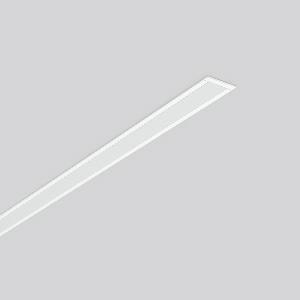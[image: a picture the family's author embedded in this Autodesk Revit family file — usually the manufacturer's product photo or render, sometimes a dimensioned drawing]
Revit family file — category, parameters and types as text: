
# Revit family: less_is_more_27_312176_002_1_76_0c9e
name_source: partatom
category: Lighting Fixtures
units: mm (PartAtom-declared; Revit-internal decimal feet)

## family parameters
Cut with Voids When Loaded = No
Host = Face
Light Source = No
Part Type = Normal
Room Calculation Point = No
Round Connector Dimension = Use Diameter
Shared = No

## types (1)
- LESS IS MORE 27 (1 x LED Modul 840, 1950 lm, 4000)
    Apparent Load = 25 VA
    CIE Flux Codes = 48 79 96 100 100
    Color Rendering = 80
    Color Temperature = 4000
    Default Elevation = 1800 mm
    Description = Series: LESS IS MORE 27
Recessed ceiling and wall luminaire with slim design. Housing: extruded aluminium profile, powder-coated. End cap aluminium powder-coated. Diffuser made of non-yellowing plastic (PMMA), opal. Suitable for Recessed ceiling mounting, wall (recessed). External driver with connecting cable. 
Colour: traffic white, matt (RAL 9016)
Length: 1014 mm
Width: 38 mm
Height: 2 mm
Cut-out length: 1006 mm
Cut-out width: 30 mm
Recess height: 45-60 mm
Luminaire: recess height: 37 mm
Lamp: LED
Socket: without socket
Colour temperature: 4000K
Colour rendering index (CRI): 82
System power: 25 W
Rated luminous flux: 1950 lm
Luminous efficiency: 78 lm/W
Control gear: Voltage converter, DALI dim.
Protection class: II
Type of protection: IP 20
    Height = 0 mm  [stored 0 ft]
    Lamp = 1 x LED Modul 840
    Lamp Light Flux = 1950 lm
    Lamp count = 1
    Length = 1014 mm
    Lifetime = 50000 h
    Luminous efficacy = 78 lm/W
    Manufacturer = RZB
    ModVariant = No
    Model = 312176.002.1.76
    Mounting Place = Ceiling, Wall
    Mounting Type = Recessed
    Number of Poles = 1
    OnlyDefault = Yes
    Power Factor = 1
    Product Name = LESS IS MORE 27
    Product group = Recessed LED linear luminaires
    ProductGroupID = 407
    Protection Class = Protection class II
    Protection Degree = IP 20
    RLX_Detail_Level = 1
    RLX_Emergency_Light_Flux = 0 lm
    RLX_Emergency_Type = 0
    RLX_Emergency_Type_DB = No
    RlxData = <blob elided: 21621 chars, md5=b4de9472>
    Socket = socket
    Standby Power = 0 W
    System Light Flux = 1950 lm
    System Power = 25 W
    Type Comments = Product without accessories
    Type Image = 312176.002.jpg
    URL = http://relux.com
    VarID = ---
    Voltage = 230 V
    Voltage Range = 220-240 V
    Weight = 0.00 kg
    Width = 38 mm

note: [stored X ft] marks values corroborated as IEEE doubles in the binary element streams (Revit-internal decimal feet)

## geometry (parser evidence)
native form markers: Blend x4, Sweep x10
no freeform markers — native parametric forms only
